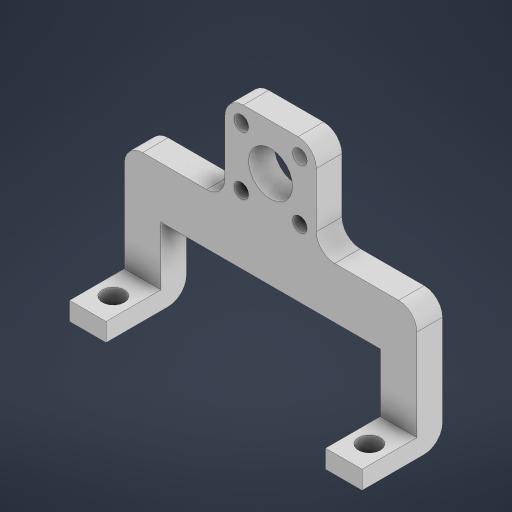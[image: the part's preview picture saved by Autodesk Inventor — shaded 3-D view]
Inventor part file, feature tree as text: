
AUTODESK INVENTOR PART (.ipt)
format: ipt  version: 2023.2 (Build 272271000, 271)  size: 264,704 bytes
history: native  units: mm
features: extrude x4, sketch x2, fillet x1
ambient origin geometry x8: Origin, YZ Plane, XZ Plane, XY Plane, X Axis, Y Axis, Z Axis, Center Point
bodies: Volumenkörper1 (feature_tree)
feature tree (7):
  sketch  "Skizze1"  dims[d0=80.0mm d1=7.0mm]
  extrude  "Extrusion1"  Depth=7.0mm
  extrude  "Extrusion2"  Depth=10.0mm
  extrude  "Extrusion3"  Depth=15.0mm
  extrude  "Extrusion4"  Depth=6.0mm
  fillet  "Rundung1"  Radius=7.0mm
  sketch  "Skizze2"  dims[d2=60.0mm d3=0.0mm d4=10.0mm d5=15.0mm d6=6.0mm d7=7.0mm d8=5.0mm d9=5.0mm d10=0.0mm d11=21.0mm d12=0.0mm d14=4.0mm d15=47.5mm d16=8.0mm d17=8.0mm d18=20.0mm d20=16.0mm d21=20.0mm d23=16.0mm d26=12.0mm d27=25.0mm d28=20.0mm d29=0.0mm d30=5.0mm]
